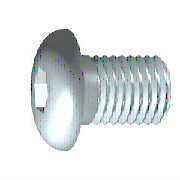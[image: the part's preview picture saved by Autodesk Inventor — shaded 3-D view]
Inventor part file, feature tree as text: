
AUTODESK INVENTOR PART (.ipt)
format: ipt  version: 2013 (Build 170138000, 138)  size: 183,808 bytes
history: native  units: mm (DEFAULTED — no unit token found)
features: sketch x2, extrude x1, plane x1
ambient origin geometry x7: Origin, YZ Plane, XY Plane, X Axis, Y Axis, Z Axis, Center Point
bodies: Solid1 (feature_tree), Body (feature_tree)
feature tree (4):
  extrude  "Slot"  Depth=0.49076mm
  plane  "Work Plane1"
  sketch  "Sketch1"  dims[d0=38.4mm d1=0.49076mm]
  sketch  "Sketch2"  dims[d2=2.75mm d3=1.56mm d4=60.0deg d5=5.0mm d6=5.0mm d7=3.464102mm d8=9.5mm d10=90.0deg d11=10.0mm d9=0.0mm d12=38.4mm d13=0.0mm d14=0.49076mm d15=0.49076mm d16=2.375mm d17=0.0mm d18=0.0mm d19=40.0mm d27=45.0deg d28=0.2mm d29=0.2mm]
